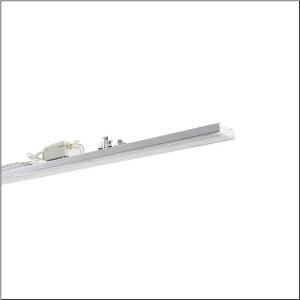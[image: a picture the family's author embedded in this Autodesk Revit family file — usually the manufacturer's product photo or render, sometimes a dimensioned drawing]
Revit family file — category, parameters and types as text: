
# Revit family: licross_11_recessed_mo_51te14dv4exg
name_source: partatom
category: Lighting Fixtures
units: mm (PartAtom-declared; Revit-internal decimal feet)

## family parameters
Cut with Voids When Loaded = No
Host = Face
Light Source = No
Part Type = Normal
Room Calculation Point = No
Round Connector Dimension = Use Diameter
Shared = No

## types (1)
- --- (1 x LED, 14140 lm, 84.1 W, 4000K)
    Apparent Load = 84 VA
    CIE Flux Codes = 56 84 97 100 100
    Color Rendering = 80
    Color Temperature = 4000K
    Default Elevation = 1800 mm
    Description = Licross 11 Recessed MO, luminaire insert, of sheet steel, galvanised, coil coated, white, length: 2.250mm, width: 66mm, height: 67mm, LED rated luminous flux: 14.140lm, light colour: 840, SDCM (Standard Deviation of Colour Matching)MacAdam ≤ 2 SDCM (initial), control gear: DALI 2, with plug, 5-pole, with phase selection, mains connection: 220..240V, AC, 50/60Hz, rated input power: 84W, internal wiring halogen-free, primary light control with lens, of plastic, primary optical cover: cover, of PMMA, light emission: direct distribution, primary light characteristic: asymmetric, protection rating (complete): IP54, insulation class (complete): insulation class I (protective earthing), certification: CE, ENEC, VDE, UKCA, protection symbol: D if used in an environment with non-conductive dust loads with corresponding accessories, impact resistance: IK06, permissible ambient temperature for indoor applications: -25..+35°C, corresponds to IFS (International Featured Standards) requirements for safety and quality in the food industry, reducing of maximum allowable ambient temperature of 5°C with ceiling mounting, LABS conformity tested according to VDMA 24364:2018-05, The light source and the operating device comply with the requirements of the Ecodesign Regulation (EU) 2019/2020 and are replaceable in accordance with this regulation, packaging unit: 1 piece
    Height = 58 mm
    Lamp = 1 x LED
    Lamp Light Flux = 14140 lm
    Lamp Power = 84.1 W
    Lamp count = 1
    Length = 2250 mm
    Luminous efficacy = 168 lm/W
    Manufacturer = Siteco
    ModVariant = No
    Model = 51TE14DV4EXG
    Mounting Place = Ceiling
    Mounting Type = Pendant
    Number of Poles = 1
    OnlyDefault = Yes
    Power Factor = 1
    Product Name = Licross 11 Recessed MO
    Product group = luminaire insert | ceiling pendant
    ProductGroupID = 901
    Protection Class = Protection class I
    Protection Degree = IP 54
    RLX_Detail_Level = 1
    RLX_Emergency_Light_Flux = 0 lm
    RLX_Emergency_Type = 0
    RLX_Emergency_Type_DB = No
    RlxData = <blob elided: 30337 chars, md5=2dbb608b>
    Socket = socket
    Standby Power = 0 W
    System Light Flux = 14140 lm
    System Power = 84 W
    Type Comments = factory setting: luminous flux: 100 % | dim-lin: 254 | 378 mA
    Type Image = l_1296930.jpg
    URL = http://relux.com
    VarID = @adj_103077
    Voltage = 0 V
    Weight = 0.00 kg
    Width = 66 mm

## geometry (parser evidence)
native form markers: Blend x4, Sweep x10
no freeform markers — native parametric forms only
